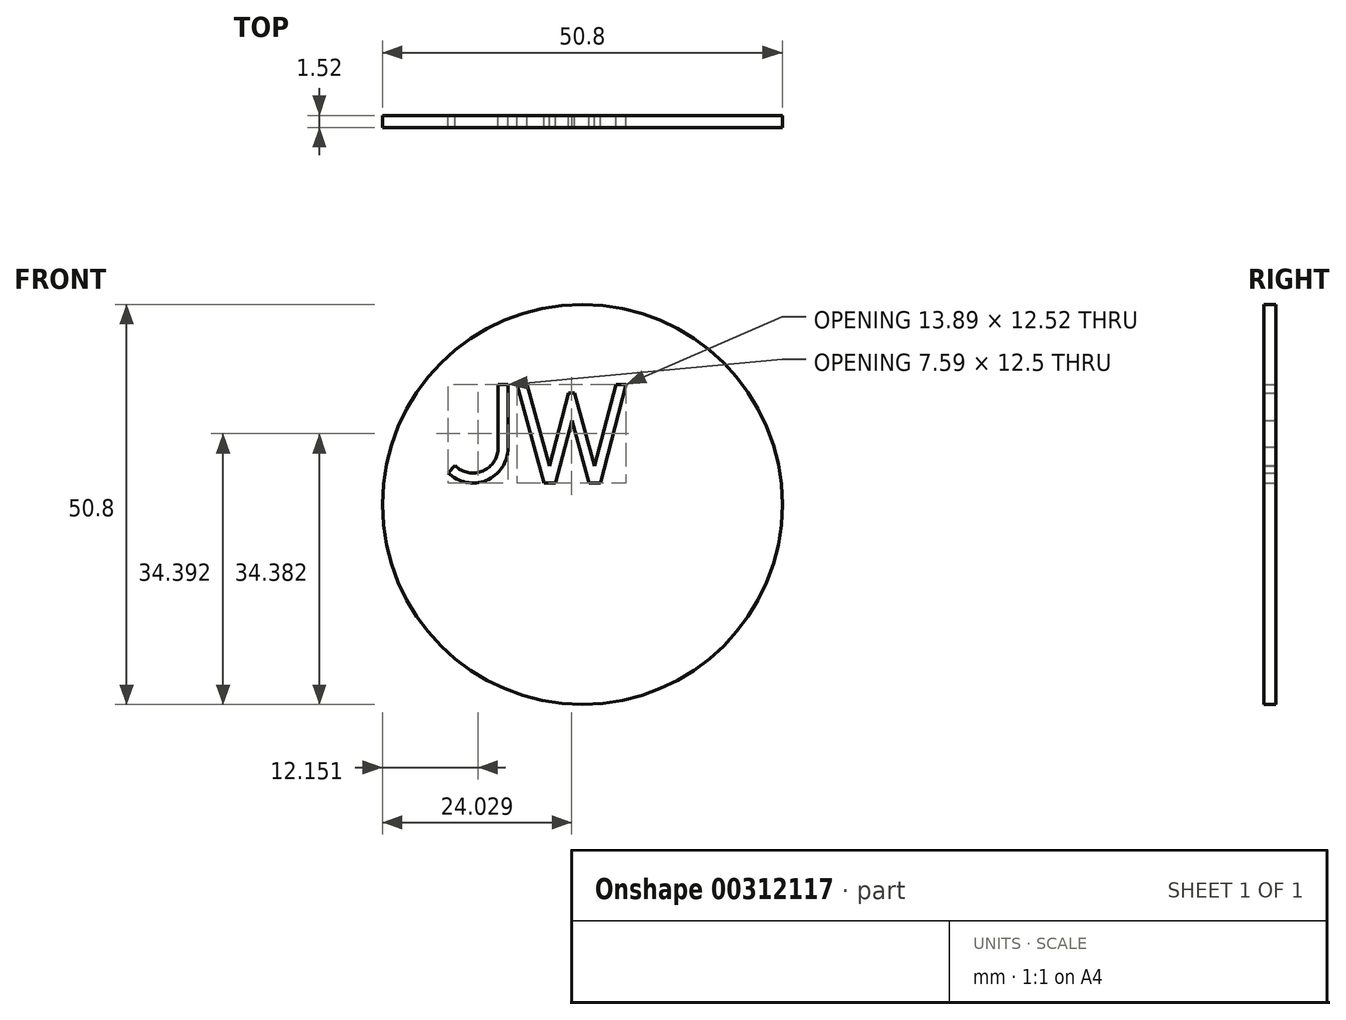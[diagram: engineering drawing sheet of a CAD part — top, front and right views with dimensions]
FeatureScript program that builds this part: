
annotation { "Feature Type Name" : "Feature", "Feature Type Description" : "" }
export const myFeature = defineFeature(function(context is Context, id is Id, definition is map)
    precondition{}
    {
        {
            var Q0;
            Q0=qCreatedBy(makeId("Front.planeOp"),FACE);
            var sketch = newSketch(context, id + "F0", { "sketchPlane" : qUnion([Q0])});
            skCircle(sketch, "E0", {"center": v(0, 0) * mm, "radius": 25.4 * mm});
            skLineSegment(sketch, "E1.bottom", {"start": v(-10.72, 15.24) * mm, "end": v(-9.45, 15.24) * mm});
            skLineSegment(sketch, "E1.right", {"start": v(-9.45, 15.24) * mm, "end": v(-9.46, 7.17) * mm});
            skArc(sketch, "E2", {"start": v(-17.05, 4.03) * mm, "mid": v(-12.2, 3.06) * mm, "end": v(-9.46, 7.17) * mm});
            skArc(sketch, "E3", {"start": v(-16.15, 4.92) * mm, "mid": v(-12.63, 4.25) * mm, "end": v(-10.72, 7.29) * mm});
            skLineSegment(sketch, "E4", {"start": v(-10.72, 7.29) * mm, "end": v(-10.72, 15.24) * mm});
            skLineSegment(sketch, "E5", {"start": v(-16.15, 4.92) * mm, "end": v(-17.05, 4.03) * mm});
            skLineSegment(sketch, "E6", {"start": v(-8.32, 15.24) * mm, "end": v(-4.88, 2.72) * mm});
            skLineSegment(sketch, "E7", {"start": v(-3.42, 2.72) * mm, "end": v(-1.34, 10.68) * mm});
            skLineSegment(sketch, "E8", {"start": v(-1.34, 10.68) * mm, "end": v(0.84, 2.72) * mm});
            skLineSegment(sketch, "E9", {"start": v(2.3, 2.72) * mm, "end": v(5.58, 15.24) * mm});
            skLineSegment(sketch, "E10", {"start": v(-8.32, 15.24) * mm, "end": v(-7, 15.24) * mm});
            skLineSegment(sketch, "E11", {"start": v(-7, 15.24) * mm, "end": v(-4.16, 4.9) * mm});
            skLineSegment(sketch, "E12", {"start": v(-4.16, 4.9) * mm, "end": v(-1.75, 14.15) * mm});
            skLineSegment(sketch, "E13", {"start": v(-1.75, 14.15) * mm, "end": v(-0.98, 14.15) * mm});
            skLineSegment(sketch, "E14", {"start": v(-0.98, 14.15) * mm, "end": v(1.56, 4.9) * mm});
            skLineSegment(sketch, "E15", {"start": v(5.58, 15.24) * mm, "end": v(4.26, 15.24) * mm});
            skLineSegment(sketch, "E16", {"start": v(4.26, 15.24) * mm, "end": v(1.56, 4.9) * mm});
            skPoint(sketch, "E17.orphan", {"position": v(-4.13, 4.8) * mm});
            skLineSegment(sketch, "E18", {"start": v(-4.88, 2.72) * mm, "end": v(-3.42, 2.72) * mm});
            skLineSegment(sketch, "E19", {"start": v(0.84, 2.72) * mm, "end": v(2.3, 2.72) * mm});
            skPoint(sketch, "E20.orphan", {"position": v(-4.13, 0) * mm});
            skPoint(sketch, "E21.orphan", {"position": v(1.6, 0) * mm});
            skSolve(sketch);
        }
        {
            var Q0;
            Q0=makeQuery(id+"F0.imprint","IMPRINT",FACE,{"disambiguationData":[TD([[makeQuery(id+"F0.imprint","IMPRINT",EDGE,{"derivedFrom":sQuery(id+"F0.wireOp",EDGE,"E0")}),1.0]])]});
            extrude(context, id + "F1", {"entities" : qUnion([Q0]), "depth" : 1.52 * mm});
        }
    });
